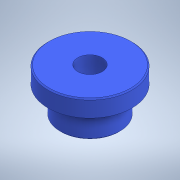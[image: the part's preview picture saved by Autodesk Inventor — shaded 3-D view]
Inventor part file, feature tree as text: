
AUTODESK INVENTOR PART (.ipt)
format: ipt  version: 2022 (Build 260153000, 153)  size: 132,608 bytes
history: native  units: mm
features: extrude x2, chamfer x2, sketch x2, projected_geometry x1
ambient origin geometry x8: Origin, YZ Plane, XZ Plane, XY Plane, X Axis, Y Axis, Z Axis, Center Point
bodies: Solid1 (feature_tree)
feature tree (7):
  extrude  "Extrusion1"  Depth=25.0mm
  extrude  "Extrusion2"  Depth=7.0mm
  chamfer  "Chamfer1"  Distance=7.0mm
  chamfer  "Chamfer2"  Distance=0.5mm Angle=45.0deg
  sketch  "Sketch1"  dims[d0=10.2mm d1=25.0mm]
  sketch  "Sketch2"  dims[d2=11.35mm d3=0.0mm d4=35.0mm d5=7.0mm d6=0.0mm d7=0.5mm d8=2.0mm d9=45.0deg d10=0.5mm d11=2.0mm d12=45.0deg]
  projected_geometry  "Projected Loop1"
